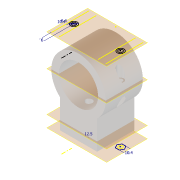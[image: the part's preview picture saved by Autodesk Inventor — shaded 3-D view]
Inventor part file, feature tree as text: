
AUTODESK INVENTOR PART (.ipt)
format: ipt  version: 2021 (Build 250183000, 183)  size: 211,456 bytes
history: native  units: mm
features: other x7, extrude x5, sketch x2, split x1, hole x1, imported_body x1
ambient origin geometry x8: Origin, YZ Plane, XZ Plane, XY Plane, X Axis, Y Axis, Z Axis, Center Point
bodies: Solid1 (feature_tree)
feature tree (17):
  extrude  "Extrusion1"  Depth=85.0mm
  other  "BoltPlane"
  other  "BoltHoles"
  extrude  "Extrusion2"  Depth=62.0mm
  extrude  "Extrusion3"  Depth=62.0mm TaperAngle=0.0deg
  other  "NutPlane"
  other  "NutHoles"
  extrude  "Extrusion4"  Depth=62.0mm
  other  "SplitPlane"
  split  "Split2"
  hole  "Hole2"  [1 undecoded]
  sketch  "Sketch4"  dims[d2=75.866mm d3=29.0mm d4=58.0mm d5=0.0mm d6=50.0mm d7=6.0mm d8=6.4mm d9=10.4mm d10=58.0mm d11=0.0mm d12=40.0mm d13=0.0mm d14=-80.0mm d15=10.4mm d16=70.0mm d17=0.0mm d18=0.0mm d28=12.5mm d29=6.2mm d30=6.0mm d31=4.0mm d32=2.0mm d33=90.0deg d34=8.0mm d35=0.0mm d36=10.2mm d37=10.2mm d38=18.0mm d39=62.0mm d40=0.0mm]
  other  "BoltHeadLevel"
  extrude  "Extrusion5"  Depth=62.0mm
  sketch  "Sketch1"  dims[d0=61.0mm d1=85.0mm]
  other  "UPPER"
  imported_body  "BASE"
note: 1 required parameter value undecoded (feature->parameter linkage not recoverable at this tier; creation-order binding heuristic only, values carry confidence <= 0.55)
